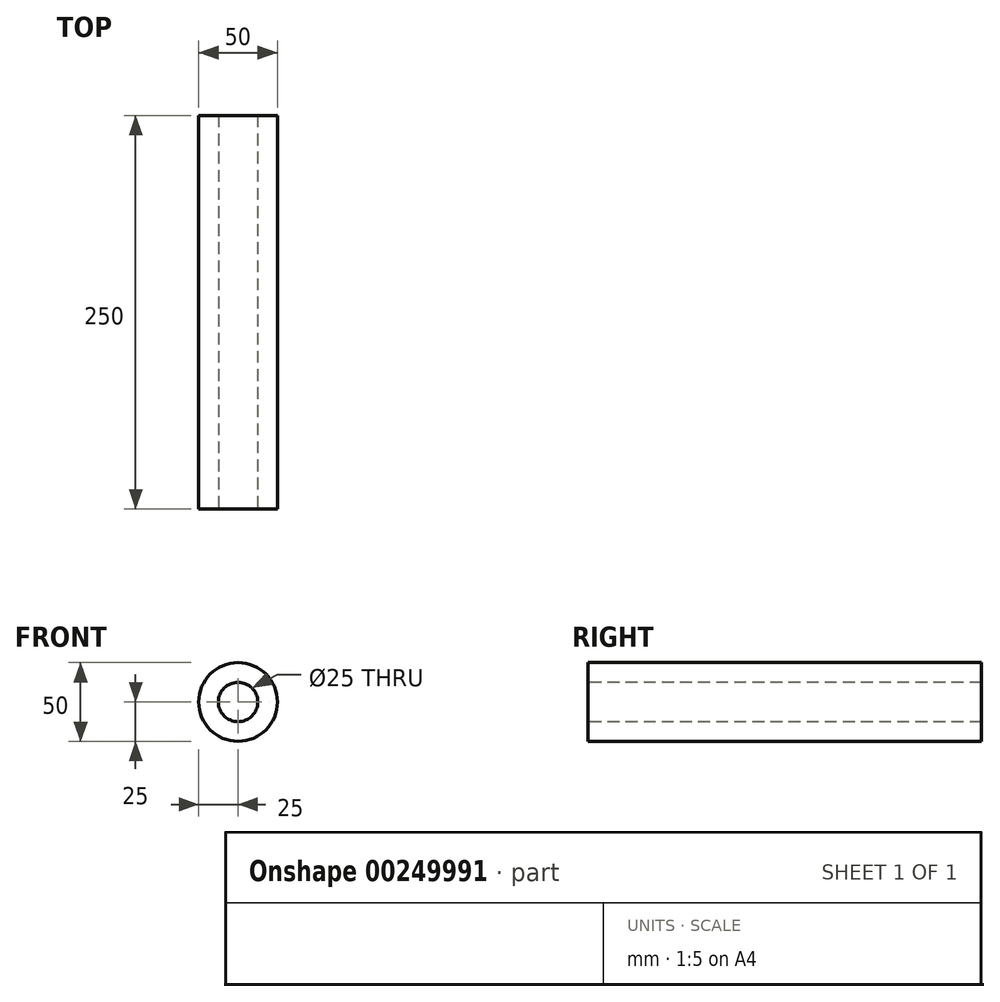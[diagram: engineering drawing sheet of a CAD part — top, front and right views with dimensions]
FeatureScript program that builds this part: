
annotation { "Feature Type Name" : "Feature", "Feature Type Description" : "" }
export const myFeature = defineFeature(function(context is Context, id is Id, definition is map)
    precondition{}
    {
        {
            var Q0;
            Q0=qCreatedBy(makeId("Front.planeOp"),FACE);
            var sketch = newSketch(context, id + "F0", { "sketchPlane" : qUnion([Q0])});
            skCircle(sketch, "E0", {"center": v(0, 0) * mm, "radius": 25 * mm});
            skSolve(sketch);
        }
        {
            var Q0;
            Q0=makeQuery(id+"F0.imprint","IMPRINT",FACE,{"disambiguationData":[TD([[makeQuery(id+"F0.imprint","IMPRINT",EDGE,{"derivedFrom":sQuery(id+"F0.wireOp",EDGE,"E0")}),1.0]])]});
            extrude(context, id + "F1", {"entities" : qUnion([Q0]), "flatOperationType" : FlatOperationType.REMOVE, "offsetDistance" : 25 * mm, "depth" : 250 * mm, "domain" : OperationDomain.MODEL});
        }
        {
            var Q0;
            Q0=makeQuery(id+"F1.opExtrude","CAP_FACE",FACE,{"disambiguationData":[OSD([sQuery(id+"F0.wireOp",EDGE,"E0")])],"isStart":false});
            var sketch = newSketch(context, id + "F2", { "sketchPlane" : qUnion([Q0])});
            skCircle(sketch, "E1", {"center": v(0, 0) * mm, "radius": 12.5 * mm});
            skSolve(sketch);
        }
        {
            var Q0;
            Q0 = qSketchRegion(id + "F2", true);
            extrude(context, id + "F3", {"entities" : qUnion([Q0]), "operationType" : NewBodyOperationType.REMOVE, "flatOperationType" : FlatOperationType.REMOVE, "endBound" : BoundingType.UP_TO_NEXT, "oppositeDirection" : true, "offsetDistance" : 25 * mm, "depth" : 50 * mm, "domain" : OperationDomain.MODEL});
        }
    });
